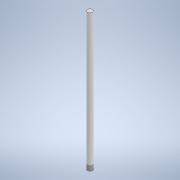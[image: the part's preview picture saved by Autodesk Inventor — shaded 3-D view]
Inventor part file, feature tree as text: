
AUTODESK INVENTOR PART (.ipt)
format: ipt  version: 2021.3 (Build 253353000, 353)  size: 93,696 bytes
history: native  units: mm
features: extrude x1, thread x1, sketch x1
ambient origin geometry x8: Origin, YZ Plane, XZ Plane, XY Plane, X Axis, Y Axis, Z Axis, Center Point
bodies: Volumenkörper1 (feature_tree)
feature tree (3):
  extrude  "Extrusion1"  Depth=160.0mm TaperAngle=0.0deg
  thread  "Gewinde1"  [1 undecoded]
  sketch  "Skizze1"  dims[d0=6.0mm d1=160.0mm d2=0.0mm d3=6.0mm d4=0.0mm]
note: 1 required parameter value undecoded (feature->parameter linkage not recoverable at this tier; creation-order binding heuristic only, values carry confidence <= 0.55)
